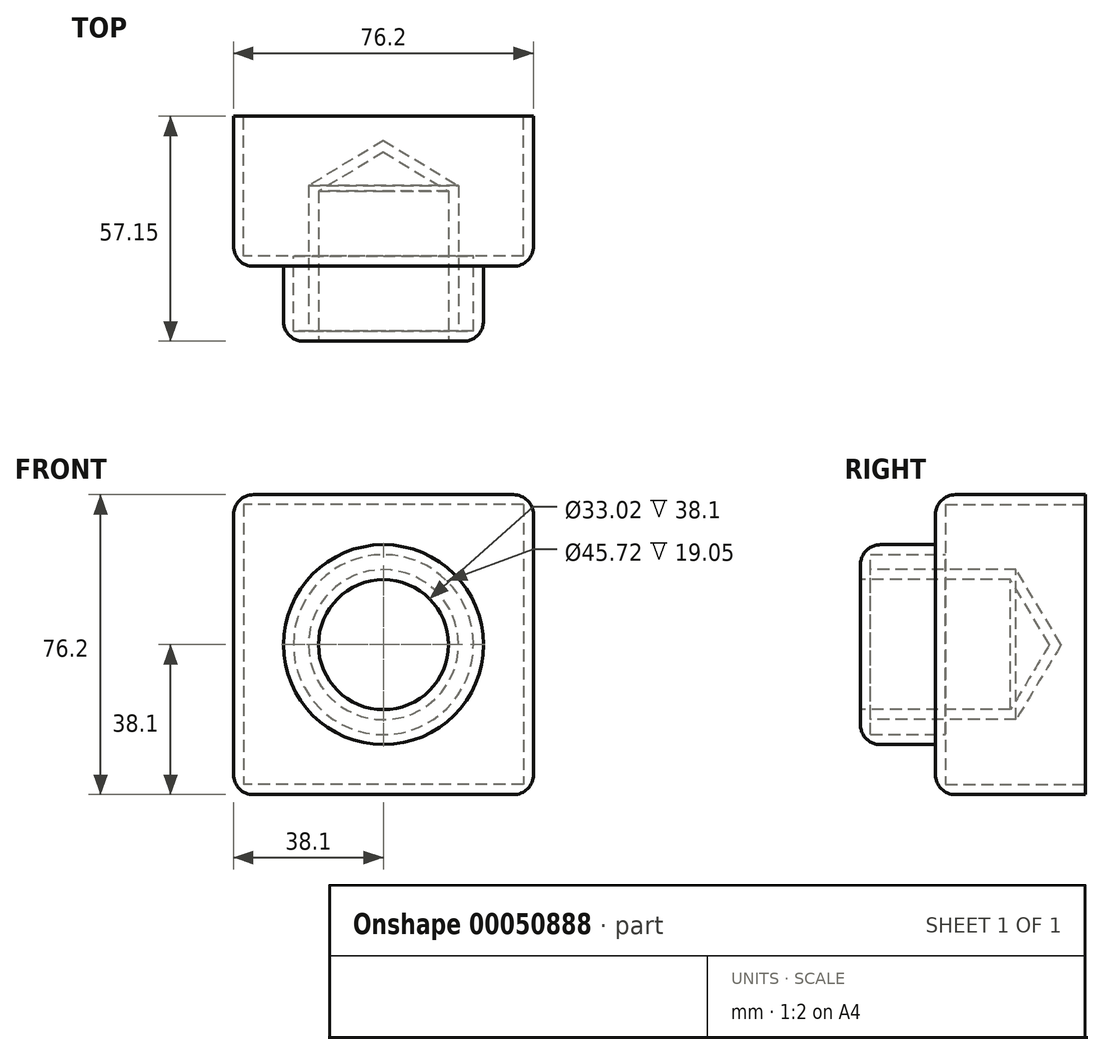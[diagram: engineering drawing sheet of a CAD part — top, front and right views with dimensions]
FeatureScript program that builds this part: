
annotation { "Feature Type Name" : "Feature", "Feature Type Description" : "" }
export const myFeature = defineFeature(function(context is Context, id is Id, definition is map)
    precondition{}
    {
        {
            var Q0;
            Q0=qCreatedBy(makeId("Front.planeOp"),FACE);
            var sketch = newSketch(context, id + "F0", { "sketchPlane" : qUnion([Q0])});
            skLineSegment(sketch, "E0.bottom", {"start": v(0, 0) * mm, "end": v(-76.2, 0) * mm});
            skLineSegment(sketch, "E0.top", {"start": v(0, -76.2) * mm, "end": v(-76.2, -76.2) * mm});
            skLineSegment(sketch, "E0.left", {"start": v(0, 0) * mm, "end": v(0, -76.2) * mm});
            skLineSegment(sketch, "E0.right", {"start": v(-76.2, 0) * mm, "end": v(-76.2, -76.2) * mm});
            skSolve(sketch);
        }
        {
            var Q0;
            Q0=makeQuery(id+"F0.imprint","IMPRINT",FACE,{"disambiguationData":[TD([[makeQuery(id+"F0.imprint","IMPRINT",EDGE,{"derivedFrom":sQuery(id+"F0.wireOp",EDGE,"E0.bottom")}),1.0]])]});
            extrude(context, id + "F1", {"entities" : qUnion([Q0]), "depth" : 38.1 * mm});
        }
        {
            var Q0;
            Q0=makeQuery(id+"F1.opExtrude","CAP_FACE",FACE,{"disambiguationData":[OSD([sQuery(id+"F0.wireOp",EDGE,"E0.bottom"),sQuery(id+"F0.wireOp",EDGE,"E0.top"),sQuery(id+"F0.wireOp",EDGE,"E0.left"),sQuery(id+"F0.wireOp",EDGE,"E0.right")])],"isStart":false});
            var sketch = newSketch(context, id + "F2", { "sketchPlane" : qUnion([Q0])});
            skCircle(sketch, "E1", {"center": v(-38.1, -38.1) * mm, "radius": 25.4 * mm});
            skSolve(sketch);
        }
        {
            var Q0;
            Q0 = qSketchRegion(id + "F2", true);
            extrude(context, id + "F3", {"entities" : qUnion([Q0]), "operationType" : NewBodyOperationType.ADD, "depth" : 19.05 * mm});
        }
        {
            var Q0;
            Q0=makeQuery(id+"F3.opExtrude","CAP_FACE",FACE,{"disambiguationData":[OSD([sQuery(id+"F2.wireOp",EDGE,"E1")])],"isStart":false});
            var sketch = newSketch(context, id + "F4", { "sketchPlane" : qUnion([Q0])});
            skCircle(sketch, "E2", {"center": v(-38.1, -38.1) * mm, "radius": 16.51 * mm});
            skSolve(sketch);
        }
        {
            var Q0;
            Q0=sQuery(id+"F4.wireOp",VERTEX,"E2.center");
            var Q1;
            Q1=makeQuery(id+"F1.opExtrude","SWEPT_BODY",BODY,{"disambiguationData":[OSD([sQuery(id+"F0.wireOp",EDGE,"E0.bottom"),sQuery(id+"F0.wireOp",EDGE,"E0.top"),sQuery(id+"F0.wireOp",EDGE,"E0.left"),sQuery(id+"F0.wireOp",EDGE,"E0.right")])]});
            hole(context, id + "F5", {"style" : HoleStyle.SIMPLE, "holeDiameter" : 33.02 * mm, "endStyle" : HoleEndStyle.BLIND, "holeDepth" : 38.1 * mm, "locations" : qUnion([Q0]), "scope" : qUnion([Q1])});
        }
        {
            var Q0;
            Q0=makeQuery(id+"F1.opExtrude","CAP_FACE",FACE,{"disambiguationData":[OSD([sQuery(id+"F0.wireOp",EDGE,"E0.bottom"),sQuery(id+"F0.wireOp",EDGE,"E0.top"),sQuery(id+"F0.wireOp",EDGE,"E0.left"),sQuery(id+"F0.wireOp",EDGE,"E0.right")])],"isStart":true});
            var Q1;
            Q1=makeQuery(id+"F1.opExtrude","SWEPT_BODY",BODY,{"disambiguationData":[OSD([sQuery(id+"F0.wireOp",EDGE,"E0.bottom"),sQuery(id+"F0.wireOp",EDGE,"E0.top"),sQuery(id+"F0.wireOp",EDGE,"E0.left"),sQuery(id+"F0.wireOp",EDGE,"E0.right")])]});
            shell(context, id + "F6", {"entities" : qUnion([Q0]), "parts" : qUnion([Q1]), "thickness" : 2.54 * mm});
        }
        {
            var Q0;
            Q0=makeQuery(id+"F1.opExtrude","CAP_EDGE",EDGE,{"disambiguationData":[OSD([sQuery(id+"F0.wireOp",EDGE,"E0.right")])],"isStart":false});
            var Q1;
            Q1=makeQuery(id+"F1.opExtrude","CAP_EDGE",EDGE,{"disambiguationData":[OSD([sQuery(id+"F0.wireOp",EDGE,"E0.bottom")])],"isStart":false});
            var Q2;
            Q2=makeQuery(id+"F1.opExtrude","CAP_EDGE",EDGE,{"disambiguationData":[OSD([sQuery(id+"F0.wireOp",EDGE,"E0.left")])],"isStart":false});
            var Q3;
            Q3=makeQuery(id+"F1.opExtrude","CAP_EDGE",EDGE,{"disambiguationData":[OSD([sQuery(id+"F0.wireOp",EDGE,"E0.top")])],"isStart":false});
            fillet(context, id + "F7", {"entities" : qUnion([Q0, Q1, Q2, Q3]), "radius" : 5.08 * mm, "tangentPropagation" : true, "allowEdgeOverflow" : false});
        }
        {
            var Q0;
            Q0=makeQuery(id+"F3.opExtrude","CAP_EDGE",EDGE,{"disambiguationData":[OSD([sQuery(id+"F2.wireOp",EDGE,"E1")])],"isStart":false});
            fillet(context, id + "F8", {"entities" : qUnion([Q0]), "radius" : 5.08 * mm, "tangentPropagation" : true, "allowEdgeOverflow" : false});
        }
        {
            var Q0;
            Q0=makeQuery(id+"F1.opExtrude","SWEPT_EDGE",EDGE,{"disambiguationData":[OSD([sQuery(id+"F0.wireOp",EDGE,"E0.bottom"),sQuery(id+"F0.wireOp",EDGE,"E0.left")])]});
            var Q1;
            Q1=makeQuery(id+"F1.opExtrude","SWEPT_EDGE",EDGE,{"disambiguationData":[OSD([sQuery(id+"F0.wireOp",EDGE,"E0.top"),sQuery(id+"F0.wireOp",EDGE,"E0.left")])]});
            var Q2;
            Q2=makeQuery(id+"F1.opExtrude","SWEPT_EDGE",EDGE,{"disambiguationData":[OSD([sQuery(id+"F0.wireOp",EDGE,"E0.bottom"),sQuery(id+"F0.wireOp",EDGE,"E0.right")])]});
            var Q3;
            Q3=makeQuery(id+"F1.opExtrude","SWEPT_EDGE",EDGE,{"disambiguationData":[OSD([sQuery(id+"F0.wireOp",EDGE,"E0.top"),sQuery(id+"F0.wireOp",EDGE,"E0.right")])]});
            fillet(context, id + "F9", {"entities" : qUnion([Q0, Q1, Q2, Q3]), "radius" : 5.08 * mm, "tangentPropagation" : true, "allowEdgeOverflow" : false});
        }
    });
